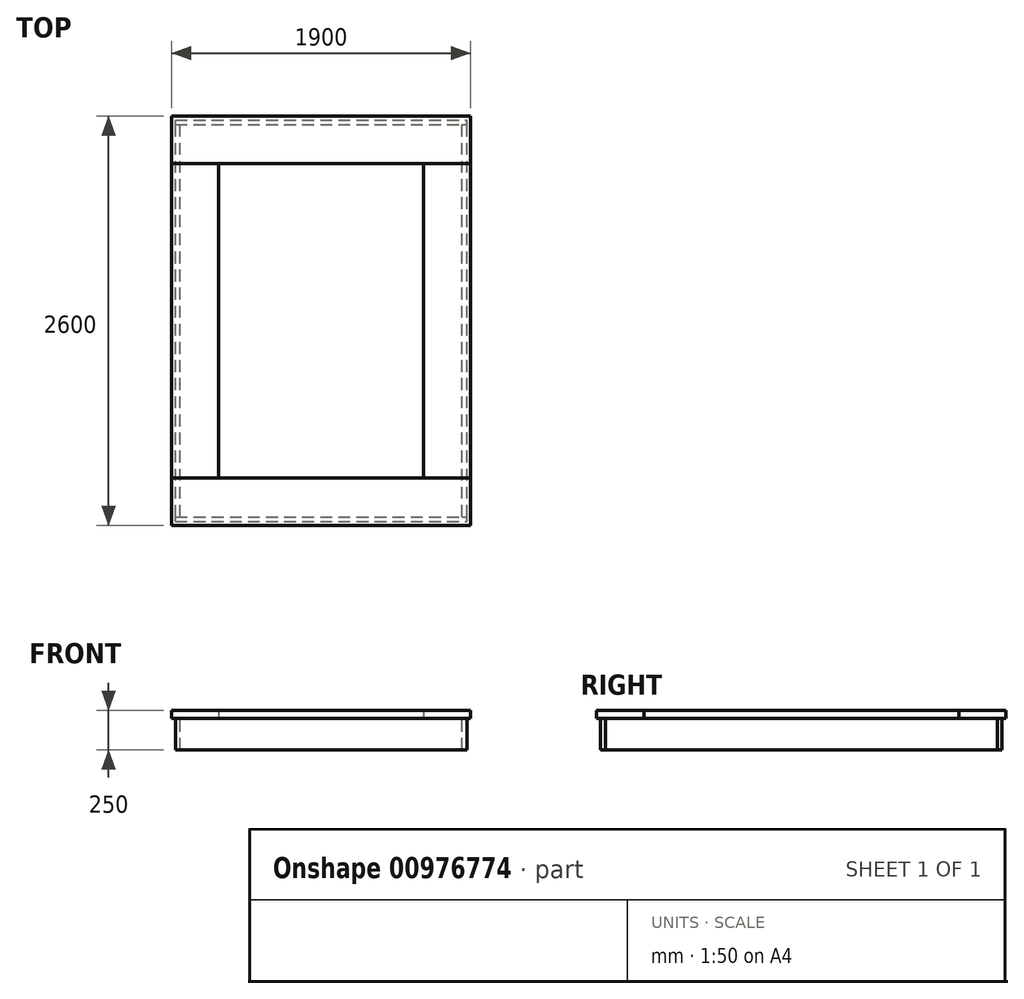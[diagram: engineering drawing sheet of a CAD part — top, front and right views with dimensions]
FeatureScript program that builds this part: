
annotation { "Feature Type Name" : "Feature", "Feature Type Description" : "" }
export const myFeature = defineFeature(function(context is Context, id is Id, definition is map)
    precondition{}
    {
        {
            var Q0;
            Q0=qCreatedBy(makeId("Top.planeOp"),FACE);
            var sketch = newSketch(context, id + "F0", { "sketchPlane" : qUnion([Q0])});
            skLineSegment(sketch, "E0.bottom", {"start": v(-950, -1300) * mm, "end": v(950, -1300) * mm});
            skLineSegment(sketch, "E0.top", {"start": v(-950, 1300) * mm, "end": v(950, 1300) * mm});
            skLineSegment(sketch, "E0.left", {"start": v(-950, -1300) * mm, "end": v(-950, 1300) * mm});
            skLineSegment(sketch, "E0.right", {"start": v(950, -1300) * mm, "end": v(950, 1300) * mm});
            skPoint(sketch, "E0.middle", {"position": v(0, 0) * mm});
            skLineSegment(sketch, "E1.0", {"start": v(-650, -1000) * mm, "end": v(-650, 1000) * mm});
            skLineSegment(sketch, "E1.1", {"start": v(-650, -1000) * mm, "end": v(650, -1000) * mm});
            skLineSegment(sketch, "E1.2", {"start": v(650, -1000) * mm, "end": v(650, 1000) * mm});
            skLineSegment(sketch, "E1.3", {"start": v(-650, 1000) * mm, "end": v(650, 1000) * mm});
            skLineSegment(sketch, "E2", {"start": v(-950, 1000) * mm, "end": v(950, 1000) * mm});
            skLineSegment(sketch, "E3", {"start": v(-950, -1000) * mm, "end": v(950, -1000) * mm});
            skLineSegment(sketch, "E4.0", {"start": v(925, -1275) * mm, "end": v(925, 1275) * mm});
            skLineSegment(sketch, "E4.1", {"start": v(-925, -1275) * mm, "end": v(925, -1275) * mm});
            skLineSegment(sketch, "E4.2", {"start": v(-925, -1275) * mm, "end": v(-925, 1275) * mm});
            skLineSegment(sketch, "E4.3", {"start": v(-925, 1275) * mm, "end": v(925, 1275) * mm});
            skLineSegment(sketch, "E5.0", {"start": v(895, -1245) * mm, "end": v(895, 1245) * mm});
            skLineSegment(sketch, "E5.1", {"start": v(-895, -1245) * mm, "end": v(895, -1245) * mm});
            skLineSegment(sketch, "E5.2", {"start": v(-895, -1245) * mm, "end": v(-895, 1245) * mm});
            skLineSegment(sketch, "E5.3", {"start": v(-895, 1245) * mm, "end": v(895, 1245) * mm});
            skLineSegment(sketch, "E6", {"start": v(-925, 1245) * mm, "end": v(925, 1245) * mm});
            skLineSegment(sketch, "E7", {"start": v(-925, -1245) * mm, "end": v(925, -1245) * mm});
            skLineSegment(sketch, "E8.0", {"start": v(-875, 1225) * mm, "end": v(875, 1225) * mm});
            skLineSegment(sketch, "E8.1", {"start": v(-875, -1225) * mm, "end": v(-875, 1225) * mm});
            skLineSegment(sketch, "E8.2", {"start": v(-875, -1225) * mm, "end": v(875, -1225) * mm});
            skLineSegment(sketch, "E8.3", {"start": v(875, -1225) * mm, "end": v(875, 1225) * mm});
            skSolve(sketch);
        }
        {
            var Q0;
            {var subQ0=sQuery(id+"F0.wireOp",EDGE,"E1.0");Q0=makeQuery(id+"F0.imprint","IMPRINT",FACE,{"disambiguationData":[TD([[makeQuery(id+"F0.imprint","IMPRINT",EDGE,{"derivedFrom":subQ0}),1.0]])]});}
            var Q1;
            {var subQ0=sQuery(id+"F0.wireOp",EDGE,"E4.2");var subQ1=sQuery(id+"F0.wireOp",EDGE,"E2");var subQ2=makeQuery(id+"F0.imprint","INTERSECT",VERTEX,{"derivedFrom":[subQ1,subQ0]});Q1=makeQuery(id+"F0.imprint","IMPRINT",FACE,{"disambiguationData":[TD([[makeQuery(id+"F0.imprint","IMPRINT",EDGE,{"disambiguationData":[TD([[subQ2,-1.0]])],"derivedFrom":subQ1}),-1.0]])]});}
            var Q2;
            {var subQ0=sQuery(id+"F0.wireOp",EDGE,"E2");var subQ1=sQuery(id+"F0.wireOp",EDGE,"E0.left");var subQ2=makeQuery(id+"F0.imprint","INTERSECT",VERTEX,{"derivedFrom":[subQ1,subQ0]});Q2=makeQuery(id+"F0.imprint","IMPRINT",FACE,{"disambiguationData":[TD([[makeQuery(id+"F0.imprint","IMPRINT",EDGE,{"disambiguationData":[TD([[subQ2,1.0]])],"derivedFrom":subQ1}),-1.0]])]});}
            var Q3;
            {var subQ0=sQuery(id+"F0.wireOp",EDGE,"E1.2");Q3=makeQuery(id+"F0.imprint","IMPRINT",FACE,{"disambiguationData":[TD([[makeQuery(id+"F0.imprint","IMPRINT",EDGE,{"derivedFrom":subQ0}),-1.0]])]});}
            var Q4;
            {var subQ0=sQuery(id+"F0.wireOp",EDGE,"E5.0");var subQ1=sQuery(id+"F0.wireOp",EDGE,"E2");var subQ2=makeQuery(id+"F0.imprint","INTERSECT",VERTEX,{"derivedFrom":[subQ1,subQ0]});Q4=makeQuery(id+"F0.imprint","IMPRINT",FACE,{"disambiguationData":[TD([[makeQuery(id+"F0.imprint","IMPRINT",EDGE,{"disambiguationData":[TD([[subQ2,-1.0]])],"derivedFrom":subQ1}),-1.0]])]});}
            var Q5;
            {var subQ0=sQuery(id+"F0.wireOp",EDGE,"E2");var subQ1=sQuery(id+"F0.wireOp",EDGE,"E0.right");var subQ2=makeQuery(id+"F0.imprint","INTERSECT",VERTEX,{"derivedFrom":[subQ1,subQ0]});Q5=makeQuery(id+"F0.imprint","IMPRINT",FACE,{"disambiguationData":[TD([[makeQuery(id+"F0.imprint","IMPRINT",EDGE,{"disambiguationData":[TD([[subQ2,1.0]])],"derivedFrom":subQ1}),1.0]])]});}
            var Q6;
            {var subQ0=sQuery(id+"F0.wireOp",EDGE,"E8.3");var subQ1=sQuery(id+"F0.wireOp",EDGE,"E2");var subQ2=makeQuery(id+"F0.imprint","INTERSECT",VERTEX,{"derivedFrom":[subQ1,subQ0]});Q6=makeQuery(id+"F0.imprint","IMPRINT",FACE,{"disambiguationData":[TD([[makeQuery(id+"F0.imprint","IMPRINT",EDGE,{"disambiguationData":[TD([[subQ2,-1.0]])],"derivedFrom":subQ1}),-1.0]])]});}
            var Q7;
            {var subQ0=sQuery(id+"F0.wireOp",EDGE,"E5.2");var subQ1=sQuery(id+"F0.wireOp",EDGE,"E2");var subQ2=makeQuery(id+"F0.imprint","INTERSECT",VERTEX,{"derivedFrom":[subQ1,subQ0]});Q7=makeQuery(id+"F0.imprint","IMPRINT",FACE,{"disambiguationData":[TD([[makeQuery(id+"F0.imprint","IMPRINT",EDGE,{"disambiguationData":[TD([[subQ2,-1.0]])],"derivedFrom":subQ1}),-1.0]])]});}
            extrude(context, id + "F1", {"entities" : qUnion([Q0, Q1, Q2, Q3, Q4, Q5, Q6, Q7]), "depth" : 50 * mm, "offsetDistance" : 25 * mm});
        }
        {
            var Q0;
            {var subQ0=sQuery(id+"F0.wireOp",EDGE,"E2");var subQ6=makeQuery(id+"F0.imprint","INTERSECT",VERTEX,{"derivedFrom":[sQuery(id+"F0.wireOp",EDGE,"E1.0"),subQ0]});Q0=makeQuery(id+"F0.imprint","IMPRINT",FACE,{"disambiguationData":[TD([[makeQuery(id+"F0.imprint","IMPRINT",EDGE,{"disambiguationData":[TD([[subQ6,1.0]])],"derivedFrom":subQ0}),1.0]])]});}
            var Q1;
            {var subQ0=sQuery(id+"F0.wireOp",EDGE,"E4.2");var subQ1=sQuery(id+"F0.wireOp",EDGE,"E2");var subQ2=makeQuery(id+"F0.imprint","INTERSECT",VERTEX,{"derivedFrom":[subQ1,subQ0]});Q1=makeQuery(id+"F0.imprint","IMPRINT",FACE,{"disambiguationData":[TD([[makeQuery(id+"F0.imprint","IMPRINT",EDGE,{"disambiguationData":[TD([[subQ2,-1.0]])],"derivedFrom":subQ1}),1.0]])]});}
            var Q2;
            {var subQ4=sQuery(id+"F0.wireOp",EDGE,"E4.3");Q2=makeQuery(id+"F0.imprint","IMPRINT",FACE,{"disambiguationData":[TD([[makeQuery(id+"F0.imprint","IMPRINT",EDGE,{"derivedFrom":subQ4}),-1.0]])]});}
            var Q3;
            {var subQ6=sQuery(id+"F0.wireOp",EDGE,"E0.top");Q3=makeQuery(id+"F0.imprint","IMPRINT",FACE,{"disambiguationData":[TD([[makeQuery(id+"F0.imprint","IMPRINT",EDGE,{"derivedFrom":subQ6}),-1.0]])]});}
            var Q4;
            {var subQ0=sQuery(id+"F0.wireOp",EDGE,"E5.0");var subQ1=sQuery(id+"F0.wireOp",EDGE,"E2");var subQ2=makeQuery(id+"F0.imprint","INTERSECT",VERTEX,{"derivedFrom":[subQ1,subQ0]});Q4=makeQuery(id+"F0.imprint","IMPRINT",FACE,{"disambiguationData":[TD([[makeQuery(id+"F0.imprint","IMPRINT",EDGE,{"disambiguationData":[TD([[subQ2,-1.0]])],"derivedFrom":subQ1}),1.0]])]});}
            var Q5;
            {var subQ3=sQuery(id+"F0.wireOp",EDGE,"E3");var subQ6=makeQuery(id+"F0.imprint","INTERSECT",VERTEX,{"derivedFrom":[sQuery(id+"F0.wireOp",EDGE,"E1.0"),subQ3]});Q5=makeQuery(id+"F0.imprint","IMPRINT",FACE,{"disambiguationData":[TD([[makeQuery(id+"F0.imprint","IMPRINT",EDGE,{"disambiguationData":[TD([[subQ6,1.0]])],"derivedFrom":subQ3}),-1.0]])]});}
            var Q6;
            {var subQ0=sQuery(id+"F0.wireOp",EDGE,"E4.2");var subQ1=sQuery(id+"F0.wireOp",EDGE,"E3");var subQ2=makeQuery(id+"F0.imprint","INTERSECT",VERTEX,{"derivedFrom":[subQ1,subQ0]});Q6=makeQuery(id+"F0.imprint","IMPRINT",FACE,{"disambiguationData":[TD([[makeQuery(id+"F0.imprint","IMPRINT",EDGE,{"disambiguationData":[TD([[subQ2,-1.0]])],"derivedFrom":subQ1}),-1.0]])]});}
            var Q7;
            {var subQ5=sQuery(id+"F0.wireOp",EDGE,"E0.bottom");Q7=makeQuery(id+"F0.imprint","IMPRINT",FACE,{"disambiguationData":[TD([[makeQuery(id+"F0.imprint","IMPRINT",EDGE,{"derivedFrom":subQ5}),1.0]])]});}
            var Q8;
            {var subQ4=sQuery(id+"F0.wireOp",EDGE,"E4.1");Q8=makeQuery(id+"F0.imprint","IMPRINT",FACE,{"disambiguationData":[TD([[makeQuery(id+"F0.imprint","IMPRINT",EDGE,{"derivedFrom":subQ4}),1.0]])]});}
            var Q9;
            {var subQ0=sQuery(id+"F0.wireOp",EDGE,"E5.0");var subQ1=sQuery(id+"F0.wireOp",EDGE,"E3");var subQ2=makeQuery(id+"F0.imprint","INTERSECT",VERTEX,{"derivedFrom":[subQ1,subQ0]});Q9=makeQuery(id+"F0.imprint","IMPRINT",FACE,{"disambiguationData":[TD([[makeQuery(id+"F0.imprint","IMPRINT",EDGE,{"disambiguationData":[TD([[subQ2,-1.0]])],"derivedFrom":subQ1}),-1.0]])]});}
            var Q10;
            {var subQ12=sQuery(id+"F0.wireOp",EDGE,"E8.0");Q10=makeQuery(id+"F0.imprint","IMPRINT",FACE,{"disambiguationData":[TD([[makeQuery(id+"F0.imprint","IMPRINT",EDGE,{"derivedFrom":subQ12}),1.0]])]});}
            var Q11;
            {var subQ12=sQuery(id+"F0.wireOp",EDGE,"E8.2");Q11=makeQuery(id+"F0.imprint","IMPRINT",FACE,{"disambiguationData":[TD([[makeQuery(id+"F0.imprint","IMPRINT",EDGE,{"derivedFrom":subQ12}),-1.0]])]});}
            extrude(context, id + "F2", {"entities" : qUnion([Q0, Q1, Q2, Q3, Q4, Q5, Q6, Q7, Q8, Q9, Q10, Q11]), "depth" : 50 * mm, "offsetDistance" : 25 * mm});
        }
        {
            var Q0;
            {var subQ0=sQuery(id+"F0.wireOp",EDGE,"E4.2");var subQ1=sQuery(id+"F0.wireOp",EDGE,"E2");var subQ2=makeQuery(id+"F0.imprint","INTERSECT",VERTEX,{"derivedFrom":[subQ1,subQ0]});Q0=makeQuery(id+"F0.imprint","IMPRINT",FACE,{"disambiguationData":[TD([[makeQuery(id+"F0.imprint","IMPRINT",EDGE,{"disambiguationData":[TD([[subQ2,-1.0]])],"derivedFrom":subQ1}),1.0]])]});}
            var Q1;
            {var subQ0=sQuery(id+"F0.wireOp",EDGE,"E4.2");var subQ1=sQuery(id+"F0.wireOp",EDGE,"E2");var subQ2=makeQuery(id+"F0.imprint","INTERSECT",VERTEX,{"derivedFrom":[subQ1,subQ0]});Q1=makeQuery(id+"F0.imprint","IMPRINT",FACE,{"disambiguationData":[TD([[makeQuery(id+"F0.imprint","IMPRINT",EDGE,{"disambiguationData":[TD([[subQ2,-1.0]])],"derivedFrom":subQ1}),-1.0]])]});}
            var Q2;
            {var subQ0=sQuery(id+"F0.wireOp",EDGE,"E4.2");var subQ1=sQuery(id+"F0.wireOp",EDGE,"E3");var subQ2=makeQuery(id+"F0.imprint","INTERSECT",VERTEX,{"derivedFrom":[subQ1,subQ0]});Q2=makeQuery(id+"F0.imprint","IMPRINT",FACE,{"disambiguationData":[TD([[makeQuery(id+"F0.imprint","IMPRINT",EDGE,{"disambiguationData":[TD([[subQ2,-1.0]])],"derivedFrom":subQ1}),-1.0]])]});}
            var Q3;
            {var subQ0=sQuery(id+"F0.wireOp",EDGE,"E5.0");var subQ1=sQuery(id+"F0.wireOp",EDGE,"E3");var subQ2=makeQuery(id+"F0.imprint","INTERSECT",VERTEX,{"derivedFrom":[subQ1,subQ0]});Q3=makeQuery(id+"F0.imprint","IMPRINT",FACE,{"disambiguationData":[TD([[makeQuery(id+"F0.imprint","IMPRINT",EDGE,{"disambiguationData":[TD([[subQ2,-1.0]])],"derivedFrom":subQ1}),-1.0]])]});}
            var Q4;
            {var subQ0=sQuery(id+"F0.wireOp",EDGE,"E5.0");var subQ1=sQuery(id+"F0.wireOp",EDGE,"E2");var subQ2=makeQuery(id+"F0.imprint","INTERSECT",VERTEX,{"derivedFrom":[subQ1,subQ0]});Q4=makeQuery(id+"F0.imprint","IMPRINT",FACE,{"disambiguationData":[TD([[makeQuery(id+"F0.imprint","IMPRINT",EDGE,{"disambiguationData":[TD([[subQ2,-1.0]])],"derivedFrom":subQ1}),-1.0]])]});}
            var Q5;
            {var subQ0=sQuery(id+"F0.wireOp",EDGE,"E5.0");var subQ1=sQuery(id+"F0.wireOp",EDGE,"E2");var subQ2=makeQuery(id+"F0.imprint","INTERSECT",VERTEX,{"derivedFrom":[subQ1,subQ0]});Q5=makeQuery(id+"F0.imprint","IMPRINT",FACE,{"disambiguationData":[TD([[makeQuery(id+"F0.imprint","IMPRINT",EDGE,{"disambiguationData":[TD([[subQ2,-1.0]])],"derivedFrom":subQ1}),1.0]])]});}
            extrude(context, id + "F3", {"entities" : qUnion([Q0, Q1, Q2, Q3, Q4, Q5]), "oppositeDirection" : true, "depth" : 200 * mm, "offsetDistance" : 25 * mm});
        }
        {
            var Q0;
            {var subQ4=sQuery(id+"F0.wireOp",EDGE,"E4.3");Q0=makeQuery(id+"F0.imprint","IMPRINT",FACE,{"disambiguationData":[TD([[makeQuery(id+"F0.imprint","IMPRINT",EDGE,{"derivedFrom":subQ4}),-1.0]])]});}
            var Q1;
            {var subQ4=sQuery(id+"F0.wireOp",EDGE,"E4.1");Q1=makeQuery(id+"F0.imprint","IMPRINT",FACE,{"disambiguationData":[TD([[makeQuery(id+"F0.imprint","IMPRINT",EDGE,{"derivedFrom":subQ4}),1.0]])]});}
            extrude(context, id + "F4", {"entities" : qUnion([Q0, Q1]), "oppositeDirection" : true, "depth" : 200 * mm, "offsetDistance" : 25 * mm});
        }
    });
